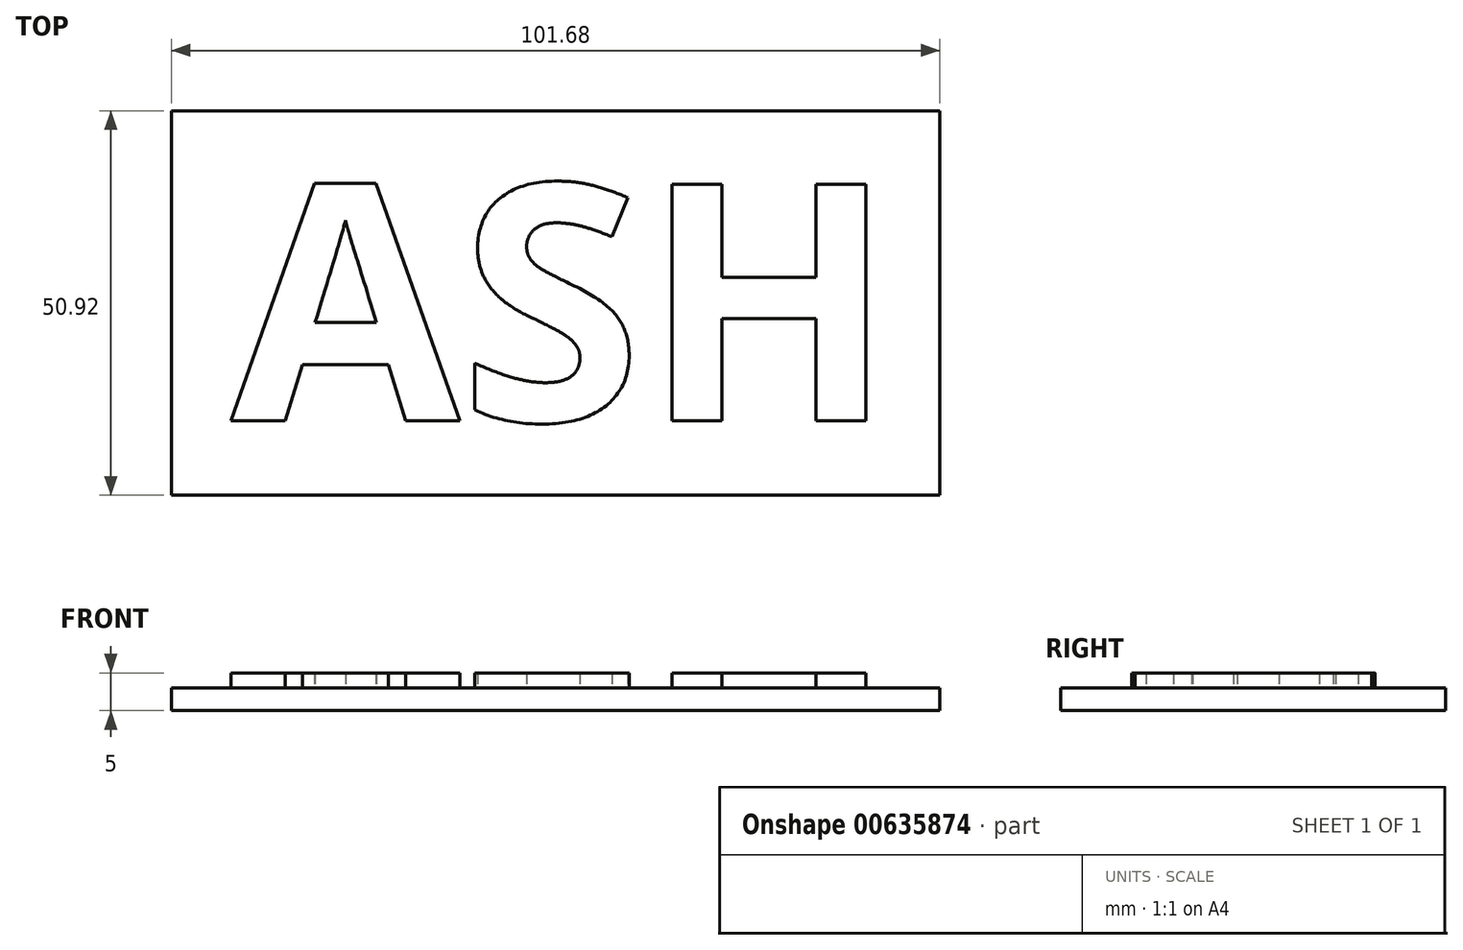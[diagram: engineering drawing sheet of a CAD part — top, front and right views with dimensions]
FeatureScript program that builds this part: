
annotation { "Feature Type Name" : "Feature", "Feature Type Description" : "" }
export const myFeature = defineFeature(function(context is Context, id is Id, definition is map)
    precondition{}
    {
        {
            var Q0;
            Q0=qCreatedBy(makeId("Top.planeOp"),FACE);
            var sketch = newSketch(context, id + "F0", { "sketchPlane" : qUnion([Q0])});
            skLineSegment(sketch, "E0.bottom", {"start": v(-46.64, 29.66) * mm, "end": v(55.04, 29.66) * mm});
            skLineSegment(sketch, "E0.top", {"start": v(-46.64, -21.26) * mm, "end": v(55.04, -21.26) * mm});
            skLineSegment(sketch, "E0.left", {"start": v(-46.64, 29.66) * mm, "end": v(-46.64, -21.26) * mm});
            skLineSegment(sketch, "E0.right", {"start": v(55.04, 29.66) * mm, "end": v(55.04, -21.26) * mm});
            skSolve(sketch);
        }
        {
            var Q0;
            Q0=makeQuery(id+"F0.imprint","IMPRINT",FACE,{"disambiguationData":[TD([[makeQuery(id+"F0.imprint","IMPRINT",EDGE,{"derivedFrom":sQuery(id+"F0.wireOp",EDGE,"E0.bottom")}),-1.0]])]});
            extrude(context, id + "F1", {"entities" : qUnion([Q0]), "depth" : 3 * mm, "offsetDistance" : 25 * mm});
        }
        {
            var Q0;
            Q0=makeQuery(id+"F1.opExtrude","CAP_FACE",FACE,{"disambiguationData":[OSD([sQuery(id+"F0.wireOp",EDGE,"E0.bottom"),sQuery(id+"F0.wireOp",EDGE,"E0.top"),sQuery(id+"F0.wireOp",EDGE,"E0.left"),sQuery(id+"F0.wireOp",EDGE,"E0.right")])],"isStart":false});
            var sketch = newSketch(context, id + "F2", { "sketchPlane" : qUnion([Q0])});
            skText(sketch, "E1", { "text": "ASH", "fontName": "OpenSans-Bold.ttf"});
            const initialGuessF2  = {"E1": [-0.03872, -0.0114, 1, 0, 0.03156]};
            skSetInitialGuess(sketch, initialGuessF2);
            skSolve(sketch);
        }
        {
            var Q0;
            Q0 = qSketchRegion(id + "F2", true);
            extrude(context, id + "F3", {"entities" : qUnion([Q0]), "operationType" : NewBodyOperationType.ADD, "depth" : 2 * mm, "offsetDistance" : 25 * mm});
        }
    });
